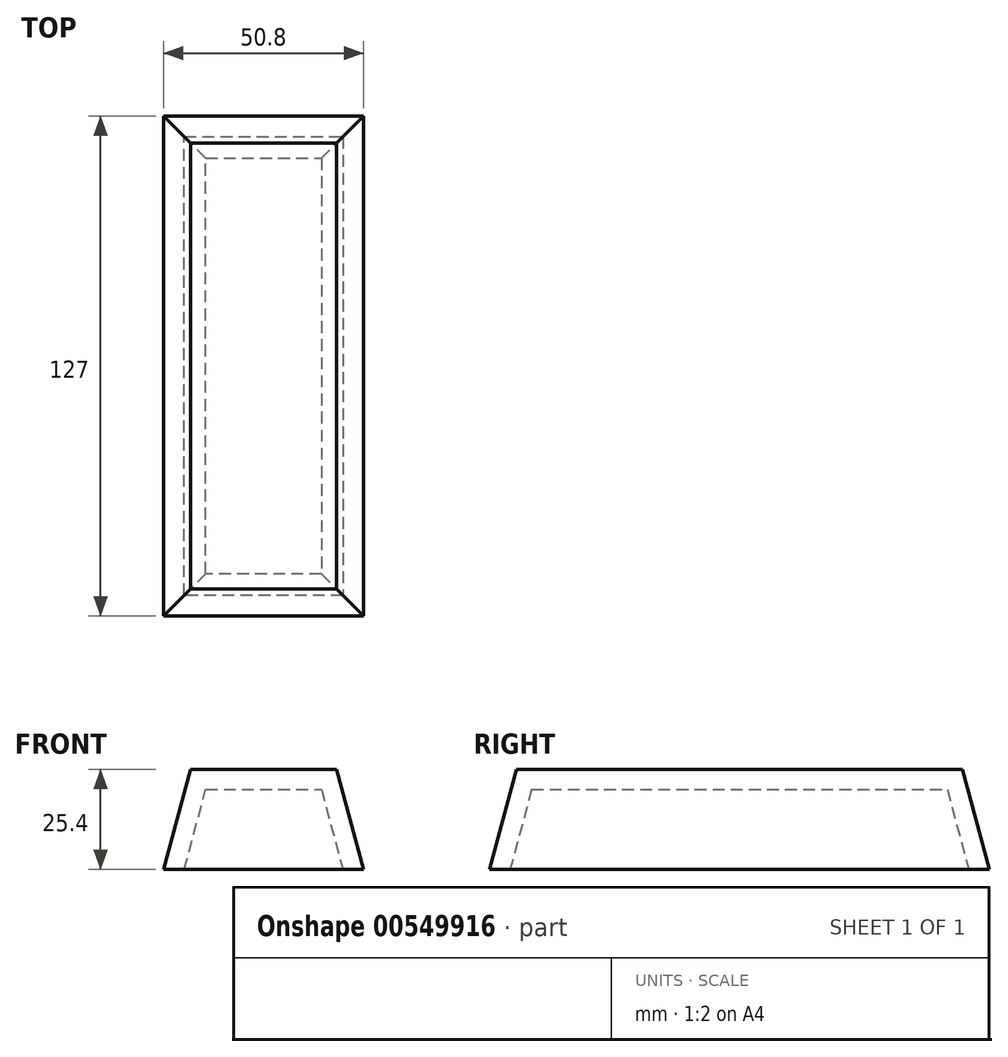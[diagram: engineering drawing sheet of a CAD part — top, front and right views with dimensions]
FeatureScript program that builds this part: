
annotation { "Feature Type Name" : "Feature", "Feature Type Description" : "" }
export const myFeature = defineFeature(function(context is Context, id is Id, definition is map)
    precondition{}
    {
        {
            var Q0;
            Q0=qCreatedBy(makeId("Top.planeOp"),FACE);
            var sketch = newSketch(context, id + "F0", { "sketchPlane" : qUnion([Q0])});
            skLineSegment(sketch, "E0.bottom", {"start": v(-25.4, 63.5) * mm, "end": v(25.4, 63.5) * mm});
            skLineSegment(sketch, "E0.top", {"start": v(-25.4, -63.5) * mm, "end": v(25.4, -63.5) * mm});
            skLineSegment(sketch, "E0.left", {"start": v(-25.4, 63.5) * mm, "end": v(-25.4, -63.5) * mm});
            skLineSegment(sketch, "E0.right", {"start": v(25.4, 63.5) * mm, "end": v(25.4, -63.5) * mm});
            skPoint(sketch, "E0.middle", {"position": v(0, 0) * mm});
            skSolve(sketch);
        }
        {
            var Q0;
            Q0 = qSketchRegion(id + "F0", true);
            extrude(context, id + "F1", {"entities" : qUnion([Q0]), "depth" : 25.4 * mm, "offsetDistance" : 25.4 * mm, "hasDraft" : true, "draftAngle" : 15 * degree, "draftPullDirection" : true});
        }
        {
            var Q0;
            Q0=makeQuery(id+"F1.opExtrude","CAP_FACE",FACE,{"disambiguationData":[OSD([sQuery(id+"F0.wireOp",EDGE,"E0.bottom"),sQuery(id+"F0.wireOp",EDGE,"E0.top"),sQuery(id+"F0.wireOp",EDGE,"E0.left"),sQuery(id+"F0.wireOp",EDGE,"E0.right")])],"isStart":true});
            shell(context, id + "F2", {"entities" : qUnion([Q0]), "thickness" : 5.08 * mm});
        }
    });
